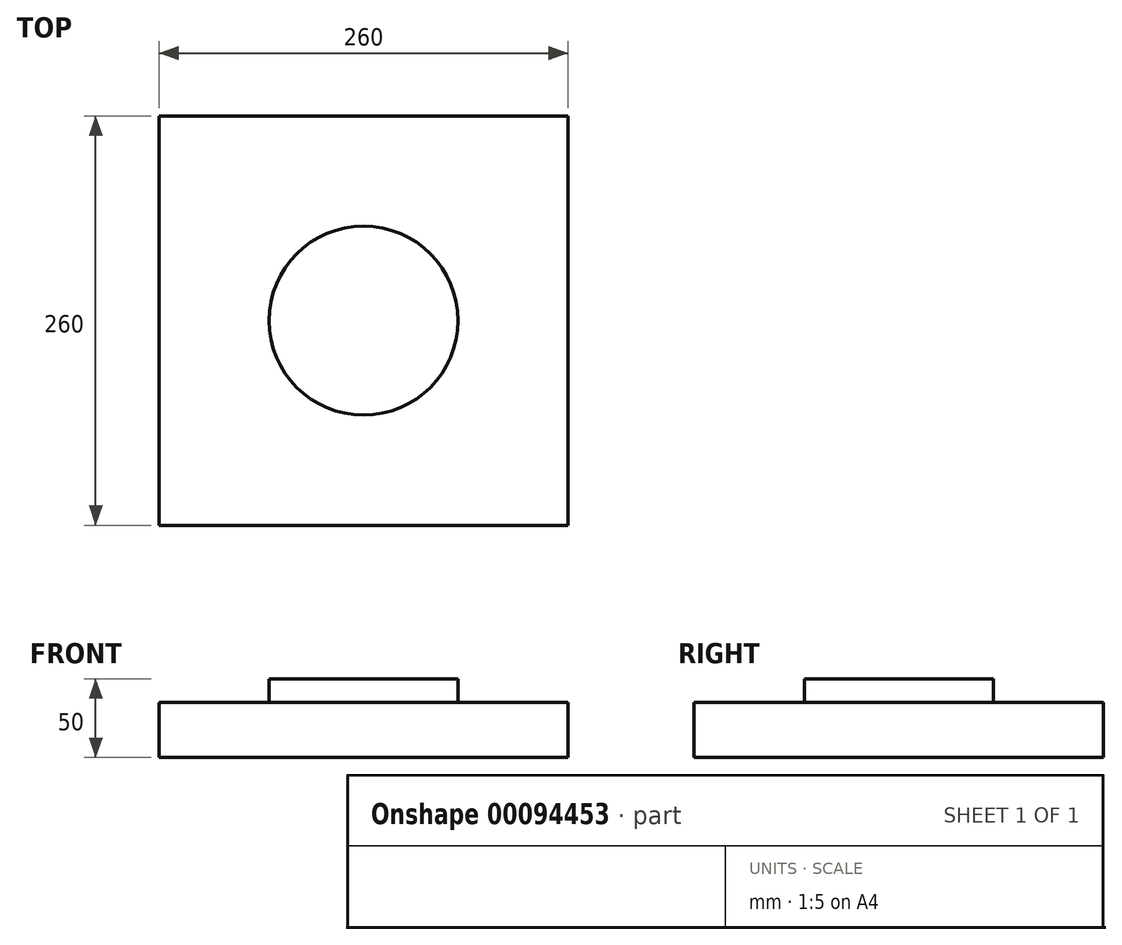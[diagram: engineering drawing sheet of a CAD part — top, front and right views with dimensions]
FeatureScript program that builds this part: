
annotation { "Feature Type Name" : "Feature", "Feature Type Description" : "" }
export const myFeature = defineFeature(function(context is Context, id is Id, definition is map)
    precondition{}
    {
        {
            var Q0;
            Q0=qCreatedBy(makeId("Top.planeOp"),FACE);
            var sketch = newSketch(context, id + "F0", { "sketchPlane" : qUnion([Q0])});
            skLineSegment(sketch, "E0", {"start": v(-118.1, 159.67) * mm, "end": v(141.9, 159.67) * mm});
            skLineSegment(sketch, "E1", {"start": v(-118.1, 159.67) * mm, "end": v(-118.1, -100.33) * mm});
            skLineSegment(sketch, "E2", {"start": v(-118.1, -100.33) * mm, "end": v(141.9, -100.33) * mm});
            skLineSegment(sketch, "E3", {"start": v(141.9, -100.33) * mm, "end": v(141.9, 159.67) * mm});
            skSolve(sketch);
        }
        {
            var Q0;
            Q0=makeQuery(id+"F0.imprint","IMPRINT",FACE,{"disambiguationData":[TD([[makeQuery(id+"F0.imprint","IMPRINT",EDGE,{"derivedFrom":sQuery(id+"F0.wireOp",EDGE,"E0")}),-1.0]])]});
            extrude(context, id + "F1", {"entities" : qUnion([Q0]), "depth" : 35 * mm});
        }
        {
            var Q0;
            Q0=makeQuery(id+"F1.opExtrude","CAP_FACE",FACE,{"disambiguationData":[OSD([sQuery(id+"F0.wireOp",EDGE,"E0"),sQuery(id+"F0.wireOp",EDGE,"E1"),sQuery(id+"F0.wireOp",EDGE,"E2"),sQuery(id+"F0.wireOp",EDGE,"E3")])],"isStart":false});
            var sketch = newSketch(context, id + "F2", { "sketchPlane" : qUnion([Q0])});
            skCircle(sketch, "E4", {"center": v(11.9, 29.67) * mm, "radius": 60 * mm});
            skPoint(sketch, "E4.centerSnap0", {"position": v(-118.1, 29.67) * mm});
            skPoint(sketch, "E4.centerSnap1", {"position": v(11.9, 159.67) * mm});
            skSolve(sketch);
        }
        {
            var Q0;
            Q0=makeQuery(id+"F2.imprint","IMPRINT",FACE,{"disambiguationData":[TD([[makeQuery(id+"F2.imprint","IMPRINT",EDGE,{"derivedFrom":sQuery(id+"F2.wireOp",EDGE,"E4")}),1.0]])]});
            extrude(context, id + "F3", {"entities" : qUnion([Q0]), "operationType" : NewBodyOperationType.ADD, "depth" : 15 * mm});
        }
    });
